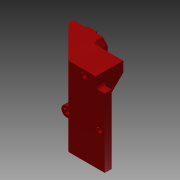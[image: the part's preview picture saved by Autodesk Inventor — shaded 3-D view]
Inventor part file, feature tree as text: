
AUTODESK INVENTOR PART (.ipt)
format: ipt  version: 2015 SP1 (Build 190203100, 203)  size: 315,904 bytes
history: native  units: in
note: dims shown in document units (in); Inventor stores cm internally (conversion verified against a paired STEP export)
features: sketch x14, extrude x9, hole x3, chamfer x3, reference x3, fillet x2
ambient origin geometry x8: Origin, YZ Plane, XZ Plane, XY Plane, X Axis, Y Axis, Z Axis, Center Point
bodies: Solid1 (feature_tree)
feature tree (34):
  sketch  "Sketch1"  dims[d0=0.7874in d1=1.5748in]
  extrude  "Extrusion1"  Depth=1.5748in
  extrude  "Extrusion6"  Depth=0.7874in
  hole  "Hole1"  [1 undecoded]
  sketch  "Sketch4"  dims[d13=0.3543in d14=0.2165in]
  extrude  "Extrusion2"  Depth=0.2165in
  extrude  "Extrusion7"  Depth=0.2461in
  extrude  "Extrusion8"  Depth=0.2461in
  fillet  "Fillet1"  Radius=0.2461in
  hole  "Hole2"  [1 undecoded]
  extrude  "Extrusion9"  Depth=0.0787in
  extrude  "Extrusion11"  Depth=0.1575in
  hole  "Hole3"  [1 undecoded]
  extrude  "Extrusion12"  Depth=0.315in TaperAngle=0.0deg
  chamfer  "Chamfer1"  [1 undecoded]
  chamfer  "Chamfer2"  Distance=0.2362in
  chamfer  "Chamfer3"  Distance=0.748in
  extrude  "Extrusion13"  Depth=0.0787in
  fillet  "Fillet4"  Radius=0.3937in
  sketch  "Sketch2"  dims[d2=0.1181in d3=0.0in d4=0.7874in]
  sketch  "Sketch3"  dims[d5=0.1772in d6=0.2362in d7=0.315in d8=0.9843in d9=90.0deg d10=0.315in d11=0.8108in d12=0.3543in]
  sketch  "Sketch5"  dims[d15=1.5748in d16=0.2461in]
  sketch  "Sketch9"  dims[d17=0.2461in d18=0.2461in d19=0.2461in]
  sketch  "Sketch10"  dims[d20=0.0394in d21=0.0in d35=45.0deg]
  sketch  "Sketch11"  dims[d37=0.0787in d38=0.0in d39=0.7874in]
  sketch  "Sketch12"  dims[d40=0.1575in d41=0.9843in]
  reference  "Reference1"
  reference  "Reference2"
  sketch  "Sketch13"  dims[d42=2.7953in d43=0.4724in]
  reference  "Reference3"
  sketch  "Sketch15"  dims[d44=0.315in d45=0.0in d46=0.315in d47=0.0in]
  sketch  "Sketch16"  dims[d48=0.0787in]
  sketch  "Sketch18"  dims[d49=0.1181in d50=0.2362in d51=0.2559in d52=0.1181in d53=90.0deg d54=0.315in d55=0.8108in d56=0.0in d57=0.0in]
  sketch  "Sketch19"  dims[d60=1.2598in d63=0.2362in d64=0.0in d69=0.748in d71=0.1181in d72=0.2362in d73=0.2559in d74=0.1181in d75=90.0deg d76=0.315in d77=0.8108in d82=0.4724in d83=0.3937in d84=0.3937in d85=0.0591in d86=0.0in d87=0.0591in d88=0.0787in d89=45.0deg d92=0.1181in d93=0.0787in d94=45.0deg d95=0.2756in d96=0.4724in d97=0.0787in d98=30.0deg d99=0.5187in d100=0.0in d101=0.0787in d102=0.1378in]
note: 4 required parameter values undecoded (feature->parameter linkage not recoverable at this tier; creation-order binding heuristic only, values carry confidence <= 0.55)
